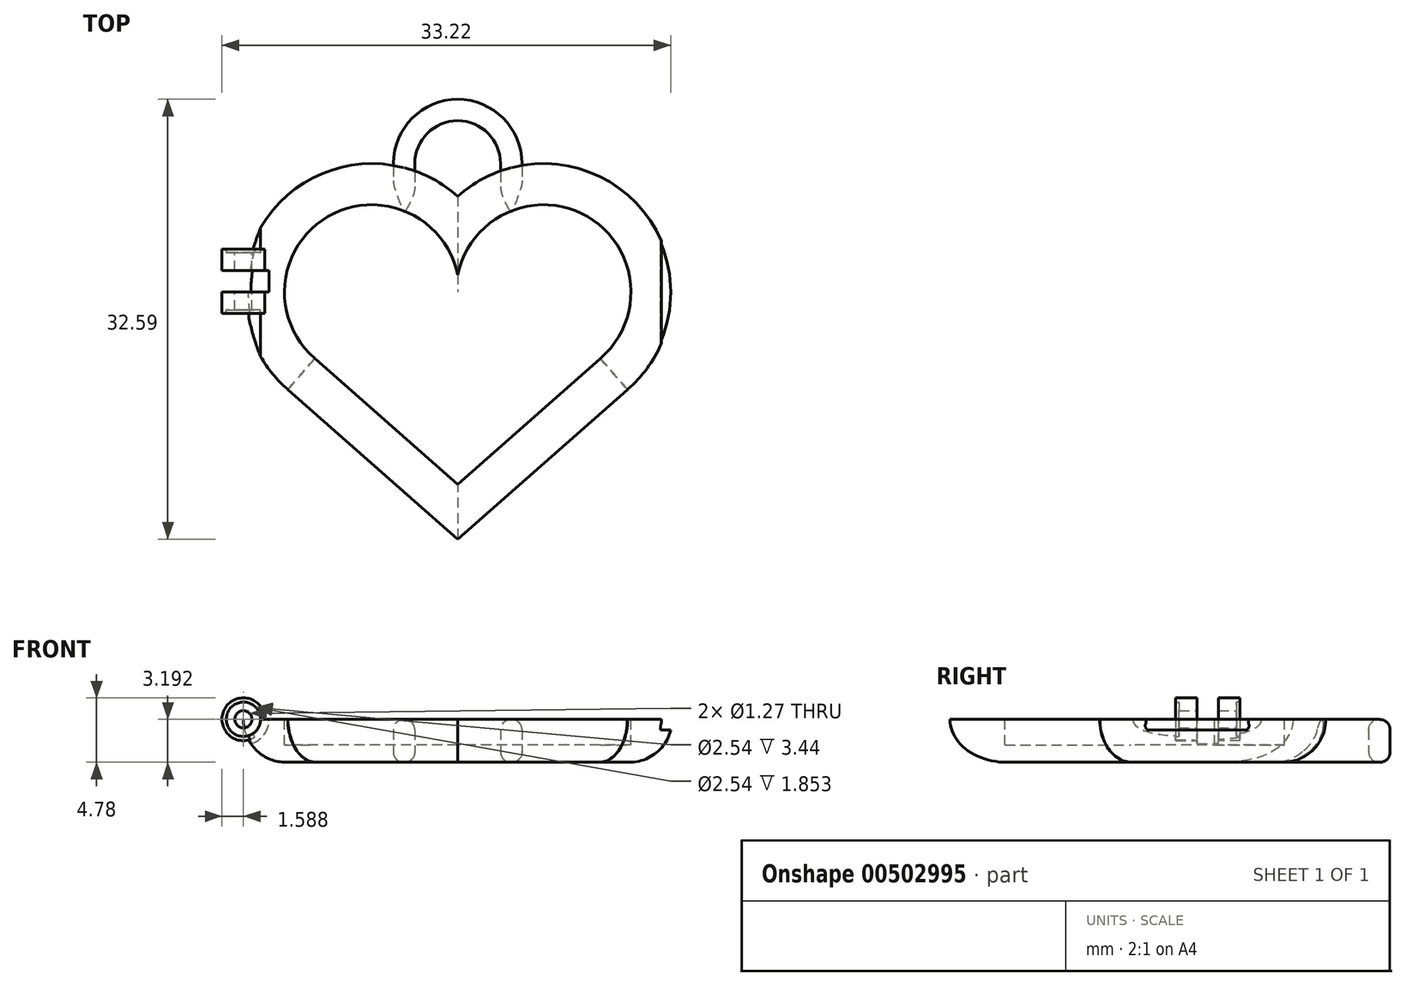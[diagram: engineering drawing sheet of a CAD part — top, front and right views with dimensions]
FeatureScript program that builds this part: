
annotation { "Feature Type Name" : "Feature", "Feature Type Description" : "" }
export const myFeature = defineFeature(function(context is Context, id is Id, definition is map)
    precondition{}
    {
        {
            var Q0;
            Q0=qCreatedBy(makeId("Top.planeOp"),FACE);
            var sketch = newSketch(context, id + "F0", { "sketchPlane" : qUnion([Q0])});
            skArc(sketch, "E0", {"start": v(0, 7.1) * mm, "mid": v(-13.5, 6.29) * mm, "end": v(-12.57, -7.21) * mm});
            skArc(sketch, "E1", {"start": v(0, 7.1) * mm, "mid": v(13.5, 6.29) * mm, "end": v(12.57, -7.21) * mm});
            skLineSegment(sketch, "E2", {"start": v(-12.57, -7.21) * mm, "end": v(0, -18.3) * mm});
            skLineSegment(sketch, "E3", {"start": v(0, -18.3) * mm, "end": v(12.57, -7.21) * mm});
            skSolve(sketch);
        }
        {
            var Q0;
            Q0=makeQuery(id+"F0.imprint","IMPRINT",FACE,{"disambiguationData":[TD([[makeQuery(id+"F0.imprint","IMPRINT",EDGE,{"derivedFrom":sQuery(id+"F0.wireOp",EDGE,"E0")}),1.0]])]});
            extrude(context, id + "F1", {"entities" : qUnion([Q0]), "depth" : 6.35 * mm});
        }
        {
            var Q0;
            Q0=makeQuery(id+"F1.opExtrude","CAP_FACE",FACE,{"disambiguationData":[OSD([sQuery(id+"F0.wireOp",EDGE,"E0"),sQuery(id+"F0.wireOp",EDGE,"E1"),sQuery(id+"F0.wireOp",EDGE,"E2"),sQuery(id+"F0.wireOp",EDGE,"E3")])],"isStart":false});
            var Q1;
            Q1=makeQuery(id+"F1.opExtrude","CAP_FACE",FACE,{"disambiguationData":[OSD([sQuery(id+"F0.wireOp",EDGE,"E0"),sQuery(id+"F0.wireOp",EDGE,"E1"),sQuery(id+"F0.wireOp",EDGE,"E2"),sQuery(id+"F0.wireOp",EDGE,"E3")])],"isStart":true});
            fillet(context, id + "F2", {"entities" : qUnion([Q0, Q1]), "radius" : 3.17 * mm, "tangentPropagation" : true, "allowEdgeOverflow" : false});
        }
        {
            var Q0;
            Q0=makeQuery(id+"F2.opFillet","BLEND_EDGE",EDGE,{"blendedFrom":[makeQuery(id+"F1.opExtrude","CAP_EDGE",EDGE,{"disambiguationData":[OSD([sQuery(id+"F0.wireOp",EDGE,"E0")])],"isStart":false}),makeQuery(id+"F1.opExtrude","CAP_EDGE",EDGE,{"disambiguationData":[OSD([sQuery(id+"F0.wireOp",EDGE,"E2")])],"isStart":false})],"blendedInto":[]});
            var Q1;
            Q1=makeQuery(id+"F2.opFillet","BLEND_EDGE",EDGE,{"blendedFrom":[makeQuery(id+"F1.opExtrude","CAP_EDGE",EDGE,{"disambiguationData":[OSD([sQuery(id+"F0.wireOp",EDGE,"E1")])],"isStart":false}),makeQuery(id+"F1.opExtrude","CAP_EDGE",EDGE,{"disambiguationData":[OSD([sQuery(id+"F0.wireOp",EDGE,"E3")])],"isStart":false})],"blendedInto":[]});
            fillet(context, id + "F3", {"entities" : qUnion([Q0, Q1]), "radius" : 2.54 * mm, "tangentPropagation" : true, "allowEdgeOverflow" : false});
        }
        {
            var Q0;
            Q0=qCreatedBy(makeId("Top.planeOp"),FACE);
            var sketch = newSketch(context, id + "F4", { "sketchPlane" : qUnion([Q0])});
            skCircle(sketch, "E4", {"center": v(0, 9.53) * mm, "radius": 3.18 * mm});
            skCircle(sketch, "E5", {"center": v(0, 9.53) * mm, "radius": 4.76 * mm});
            skLineSegment(sketch, "E6", {"start": v(-4.76, 9.53) * mm, "end": v(-4.76, 0) * mm});
            skLineSegment(sketch, "E7", {"start": v(4.76, 9.53) * mm, "end": v(4.76, 0) * mm});
            skLineSegment(sketch, "E8", {"start": v(3.18, 9.53) * mm, "end": v(3.18, 0) * mm});
            skLineSegment(sketch, "E9", {"start": v(-3.17, 9.53) * mm, "end": v(-3.17, 0) * mm});
            skLineSegment(sketch, "E10", {"start": v(-4.76, 0) * mm, "end": v(4.76, 0) * mm});
            skSolve(sketch);
        }
        {
            var Q0;
            {var subQ5=sQuery(id+"F4.wireOp",EDGE,"E8");var subQ7=sQuery(id+"F4.wireOp",EDGE,"E4");var subQ8=makeQuery(id+"F4.imprint","INTERSECT",VERTEX,{"derivedFrom":[subQ7,subQ5]});Q0=makeQuery(id+"F4.imprint","IMPRINT",FACE,{"disambiguationData":[TD([[makeQuery(id+"F4.imprint","IMPRINT",EDGE,{"disambiguationData":[TD([[subQ8,-1.0]])],"derivedFrom":subQ7}),-1.0]])]});}
            var Q1;
            {var subQ0=sQuery(id+"F4.wireOp",EDGE,"E7");Q1=makeQuery(id+"F4.imprint","IMPRINT",FACE,{"disambiguationData":[TD([[makeQuery(id+"F4.imprint","IMPRINT",EDGE,{"derivedFrom":subQ0}),-1.0]])]});}
            var Q2;
            {var subQ0=sQuery(id+"F4.wireOp",EDGE,"E6");Q2=makeQuery(id+"F4.imprint","IMPRINT",FACE,{"disambiguationData":[TD([[makeQuery(id+"F4.imprint","IMPRINT",EDGE,{"derivedFrom":subQ0}),1.0]])]});}
            extrude(context, id + "F5", {"entities" : qUnion([Q0, Q1, Q2]), "operationType" : NewBodyOperationType.ADD, "depth" : 3.17 * mm});
        }
        {
            var Q0;
            Q0=makeQuery(id+"F5.opExtrude","CAP_EDGE",EDGE,{"disambiguationData":[OSD([sQuery(id+"F4.wireOp",EDGE,"E4")])],"isStart":true});
            var Q1;
            Q1=makeQuery(id+"F5.opExtrude","CAP_EDGE",EDGE,{"disambiguationData":[OSD([sQuery(id+"F4.wireOp",EDGE,"E5")])],"isStart":true});
            var Q2;
            Q2=makeQuery(id+"F5.opExtrude","CAP_EDGE",EDGE,{"disambiguationData":[OSD([sQuery(id+"F4.wireOp",EDGE,"E5")])],"isStart":false});
            var Q3;
            Q3=makeQuery(id+"F5.opExtrude","CAP_EDGE",EDGE,{"disambiguationData":[OSD([sQuery(id+"F4.wireOp",EDGE,"E4")])],"isStart":false});
            fillet(context, id + "F6", {"entities" : qUnion([Q0, Q1, Q2, Q3]), "radius" : 0.76 * mm, "tangentPropagation" : true, "allowEdgeOverflow" : false});
        }
        {
            var Q0;
            Q0=qCreatedBy(makeId("Front.planeOp"),FACE);
            var sketch = newSketch(context, id + "F7", { "sketchPlane" : qUnion([Q0])});
            skLineSegment(sketch, "E11.bottom", {"start": v(18.97, 3.18) * mm, "end": v(-18.97, 3.18) * mm});
            skLineSegment(sketch, "E11.top", {"start": v(18.97, 9.53) * mm, "end": v(-18.97, 9.53) * mm});
            skLineSegment(sketch, "E11.left", {"start": v(18.97, 3.18) * mm, "end": v(18.97, 9.53) * mm});
            skLineSegment(sketch, "E11.right", {"start": v(-18.97, 3.18) * mm, "end": v(-18.97, 9.53) * mm});
            skPoint(sketch, "E11.middle", {"position": v(0, 6.35) * mm});
            skSolve(sketch);
        }
        {
            var Q0;
            Q0 = qSketchRegion(id + "F7", true);
            extrude(context, id + "F8", {"entities" : qUnion([Q0]), "operationType" : NewBodyOperationType.REMOVE, "endBound" : BoundingType.SYMMETRIC, "oppositeDirection" : true, "depth" : 50.8 * mm});
        }
        {
            var Q0;
            Q0=makeQuery(id+"F8.boolean.opBoolean","MERGE",FACE,{"derivedFrom":[makeQuery(id+"F5.opExtrude","CAP_FACE",FACE,{"disambiguationData":[OSD([sQuery(id+"F4.wireOp",EDGE,"E4"),sQuery(id+"F4.wireOp",EDGE,"E5"),sQuery(id+"F4.wireOp",EDGE,"E6"),sQuery(id+"F4.wireOp",EDGE,"E7"),sQuery(id+"F4.wireOp",EDGE,"E8"),sQuery(id+"F4.wireOp",EDGE,"E9"),sQuery(id+"F4.wireOp",EDGE,"E10")])],"isStart":false}),makeQuery(id+"F8.opExtrude","SWEPT_FACE",FACE,{"disambiguationData":[OSD([sQuery(id+"F7.wireOp",EDGE,"E11.bottom")])]})]});
            shell(context, id + "F9", {"entities" : qUnion([Q0]), "thickness" : 3.05 * mm});
        }
        {
            var Q0;
            Q0=makeQuery(id+"F8.boolean.opBoolean","MERGE",FACE,{"derivedFrom":[makeQuery(id+"F5.opExtrude","CAP_FACE",FACE,{"disambiguationData":[OSD([sQuery(id+"F4.wireOp",EDGE,"E4"),sQuery(id+"F4.wireOp",EDGE,"E5"),sQuery(id+"F4.wireOp",EDGE,"E6"),sQuery(id+"F4.wireOp",EDGE,"E7"),sQuery(id+"F4.wireOp",EDGE,"E8"),sQuery(id+"F4.wireOp",EDGE,"E9"),sQuery(id+"F4.wireOp",EDGE,"E10")])],"isStart":false}),makeQuery(id+"F8.opExtrude","SWEPT_FACE",FACE,{"disambiguationData":[OSD([sQuery(id+"F7.wireOp",EDGE,"E11.bottom")])]})]});
            var sketch = newSketch(context, id + "F10", { "sketchPlane" : qUnion([Q0])});
            skLineSegment(sketch, "E12", {"start": v(0, -14.24) * mm, "end": v(10.55, -4.93) * mm});
            skLineSegment(sketch, "E13", {"start": v(0, -14.24) * mm, "end": v(-10.55, -4.93) * mm});
            skArc(sketch, "E14", {"start": v(0, 1.28) * mm, "mid": v(-9.61, 5.6) * mm, "end": v(-10.59, -4.9) * mm});
            skArc(sketch, "E15", {"start": v(0, 1.28) * mm, "mid": v(9.61, 5.6) * mm, "end": v(10.59, -4.9) * mm});
            skLineSegment(sketch, "E16", {"start": v(10.55, -4.93) * mm, "end": v(10.59, -4.9) * mm});
            skLineSegment(sketch, "E17", {"start": v(-10.59, -4.9) * mm, "end": v(-10.55, -4.93) * mm});
            skSolve(sketch);
        }
        {
            var Q0;
            Q0 = qSketchRegion(id + "F10", true);
            extrude(context, id + "F11", {"entities" : qUnion([Q0]), "operationType" : NewBodyOperationType.REMOVE, "oppositeDirection" : true, "depth" : 1.9 * mm});
        }
        {
            var Q0;
            Q0=qCreatedBy(makeId("Front.planeOp"),FACE);
            var sketch = newSketch(context, id + "F12", { "sketchPlane" : qUnion([Q0])});
            skCircle(sketch, "E18", {"center": v(-15.86, 3.2) * mm, "radius": 1.59 * mm});
            skCircle(sketch, "E19", {"center": v(-15.86, 3.2) * mm, "radius": 0.64 * mm});
            skSolve(sketch);
        }
        {
            var Q0;
            Q0 = qSketchRegion(id + "F12", true);
            extrude(context, id + "F13", {"entities" : qUnion([Q0]), "operationType" : NewBodyOperationType.ADD, "depth" : 1.59 * mm});
        }
        {
            var Q0;
            Q0 = qSketchRegion(id + "F12", true);
            extrude(context, id + "F14", {"entities" : qUnion([Q0]), "operationType" : NewBodyOperationType.ADD, "oppositeDirection" : true, "depth" : 3.17 * mm, "hasSecondDirection" : true, "secondDirectionOppositeDirection" : true, "secondDirectionDepth" : 1.59 * mm});
        }
        {
            var Q0;
            Q0=makeQuery(id+"F12.imprint","IMPRINT",FACE,{"disambiguationData":[TD([[makeQuery(id+"F12.imprint","IMPRINT",EDGE,{"derivedFrom":sQuery(id+"F12.wireOp",EDGE,"E19")}),1.0]])]});
            extrude(context, id + "F15", {"entities" : qUnion([Q0]), "operationType" : NewBodyOperationType.REMOVE, "endBound" : BoundingType.SYMMETRIC, "oppositeDirection" : true, "depth" : 25.4 * mm});
        }
        {
            var Q0;
            Q0=makeQuery(id+"F13.opExtrude","CAP_FACE",FACE,{"disambiguationData":[OSD([sQuery(id+"F12.wireOp",EDGE,"E18"),sQuery(id+"F12.wireOp",EDGE,"E19")])],"isStart":false});
            var sketch = newSketch(context, id + "F16", { "sketchPlane" : qUnion([Q0])});
            skCircle(sketch, "E20", {"center": v(-15.86, 3.2) * mm, "radius": 1.27 * mm});
            skSolve(sketch);
        }
        {
            var Q0;
            Q0 = qSketchRegion(id + "F16", true);
            extrude(context, id + "F17", {"entities" : qUnion([Q0]), "operationType" : NewBodyOperationType.REMOVE, "depth" : 25.4 * mm, "hasSecondDirection" : true, "secondDirectionOppositeDirection" : true, "secondDirectionDepth" : 0.25 * mm});
        }
        {
            var Q0;
            Q0=makeQuery(id+"F14.opExtrude","CAP_FACE",FACE,{"disambiguationData":[OSD([sQuery(id+"F12.wireOp",EDGE,"E18"),sQuery(id+"F12.wireOp",EDGE,"E19")])],"isStart":false});
            var sketch = newSketch(context, id + "F18", { "sketchPlane" : qUnion([Q0])});
            skCircle(sketch, "E21", {"center": v(15.86, 3.2) * mm, "radius": 1.27 * mm});
            skSolve(sketch);
        }
        {
            var Q0;
            Q0 = qSketchRegion(id + "F18", true);
            extrude(context, id + "F19", {"entities" : qUnion([Q0]), "operationType" : NewBodyOperationType.REMOVE, "depth" : 25.4 * mm, "hasSecondDirection" : true, "secondDirectionOppositeDirection" : true, "secondDirectionDepth" : 0.25 * mm});
        }
        {
            var Q0;
            Q0=makeQuery(id+"F12.imprint","IMPRINT",FACE,{"disambiguationData":[TD([[makeQuery(id+"F12.imprint","IMPRINT",EDGE,{"derivedFrom":sQuery(id+"F12.wireOp",EDGE,"E18")}),1.0]])]});
            extrude(context, id + "F20", {"entities" : qUnion([Q0]), "operationType" : NewBodyOperationType.REMOVE, "oppositeDirection" : true, "depth" : 1.59 * mm});
        }
        {
            var Q0;
            {var subQ0=sQuery(id+"F12.wireOp",EDGE,"E19");var subQ1=sQuery(id+"F12.wireOp",EDGE,"E18");Q0=makeQuery(id+"F20.boolean.opBoolean","MERGE",FACE,{"derivedFrom":[makeQuery(id+"F14.opExtrude","CAP_FACE",FACE,{"disambiguationData":[OSD([subQ1,subQ0])],"isStart":true}),makeQuery(id+"F20.opExtrude","CAP_FACE",FACE,{"disambiguationData":[OSD([subQ1,subQ0])],"isStart":false})]});}
            var sketch = newSketch(context, id + "F21", { "sketchPlane" : qUnion([Q0])});
            skCircle(sketch, "E22", {"center": v(-15.86, 3.2) * mm, "radius": 1.9 * mm});
            skSolve(sketch);
        }
        {
            var Q0;
            Q0 = qSketchRegion(id + "F21", true);
            extrude(context, id + "F22", {"entities" : qUnion([Q0]), "operationType" : NewBodyOperationType.REMOVE, "depth" : 1.59 * mm});
        }
        {
            var Q0;
            Q0=qCreatedBy(makeId("Front.planeOp"),FACE);
            var sketch = newSketch(context, id + "F23", { "sketchPlane" : qUnion([Q0])});
            skLineSegment(sketch, "E23.bottom", {"start": v(15.08, 2.38) * mm, "end": v(16.67, 2.38) * mm});
            skLineSegment(sketch, "E23.top", {"start": v(15.08, 3.97) * mm, "end": v(16.67, 3.97) * mm});
            skLineSegment(sketch, "E23.left", {"start": v(15.08, 2.38) * mm, "end": v(15.08, 3.97) * mm});
            skLineSegment(sketch, "E23.right", {"start": v(16.67, 2.38) * mm, "end": v(16.67, 3.97) * mm});
            skPoint(sketch, "E23.middle", {"position": v(15.88, 3.18) * mm});
            skSolve(sketch);
        }
        {
            var Q0;
            Q0 = qSketchRegion(id + "F23", true);
            extrude(context, id + "F24", {"entities" : qUnion([Q0]), "operationType" : NewBodyOperationType.REMOVE, "endBound" : BoundingType.SYMMETRIC, "oppositeDirection" : true, "depth" : 25.4 * mm});
        }
        {
            var Q0;
            Q0=makeQuery(id+"F24.boolean.opBoolean","COPY",FACE,{"derivedFrom":makeQuery(id+"F24.opExtrude","SWEPT_FACE",FACE,{"disambiguationData":[OSD([sQuery(id+"F23.wireOp",EDGE,"E23.left")])]})});
            var sketch = newSketch(context, id + "F25", { "sketchPlane" : qUnion([Q0])});
            skLineSegment(sketch, "E24.bottom", {"start": v(-3.98, 2.38) * mm, "end": v(4.4, 2.38) * mm});
            skLineSegment(sketch, "E24.top", {"start": v(-3.98, 2.78) * mm, "end": v(4.4, 2.78) * mm});
            skLineSegment(sketch, "E24.left", {"start": v(-3.98, 2.38) * mm, "end": v(-3.98, 2.78) * mm});
            skLineSegment(sketch, "E24.right", {"start": v(4.4, 2.38) * mm, "end": v(4.4, 2.78) * mm});
            skSolve(sketch);
        }
        {
            var Q0;
            Q0 = qSketchRegion(id + "F25", true);
            extrude(context, id + "F26", {"entities" : qUnion([Q0]), "operationType" : NewBodyOperationType.REMOVE, "oppositeDirection" : true, "depth" : 0.06 * mm});
        }
        {
            var Q0;
            Q0=makeQuery(id+"F26.boolean.opBoolean","COPY",EDGE,{"derivedFrom":makeQuery(id+"F26.opExtrude","CAP_EDGE",EDGE,{"disambiguationData":[OSD([sQuery(id+"F25.wireOp",EDGE,"E24.top")])],"isStart":false})});
            fillet(context, id + "F27", {"entities" : qUnion([Q0]), "radius" : 0.06 * mm, "tangentPropagation" : true, "allowEdgeOverflow" : false});
        }
        {
            var Q0;
            Q0=makeQuery(id+"F27.opFillet","BLEND_EDGE",EDGE,{"blendedFrom":[makeQuery(id+"F26.boolean.opBoolean","COPY",EDGE,{"derivedFrom":makeQuery(id+"F26.opExtrude","CAP_EDGE",EDGE,{"disambiguationData":[OSD([sQuery(id+"F25.wireOp",EDGE,"E24.top")])],"isStart":false})}),makeQuery(id+"F24.boolean.opBoolean","COPY",FACE,{"derivedFrom":makeQuery(id+"F24.opExtrude","SWEPT_FACE",FACE,{"disambiguationData":[OSD([sQuery(id+"F23.wireOp",EDGE,"E23.left")])]})})],"blendedInto":[makeQuery(id+"F24.boolean.opBoolean","COPY",FACE,{"derivedFrom":makeQuery(id+"F24.opExtrude","SWEPT_FACE",FACE,{"disambiguationData":[OSD([sQuery(id+"F23.wireOp",EDGE,"E23.left")])]})})]});
            fillet(context, id + "F28", {"entities" : qUnion([Q0]), "radius" : 0.64 * mm, "tangentPropagation" : true, "allowEdgeOverflow" : false});
        }
    });
